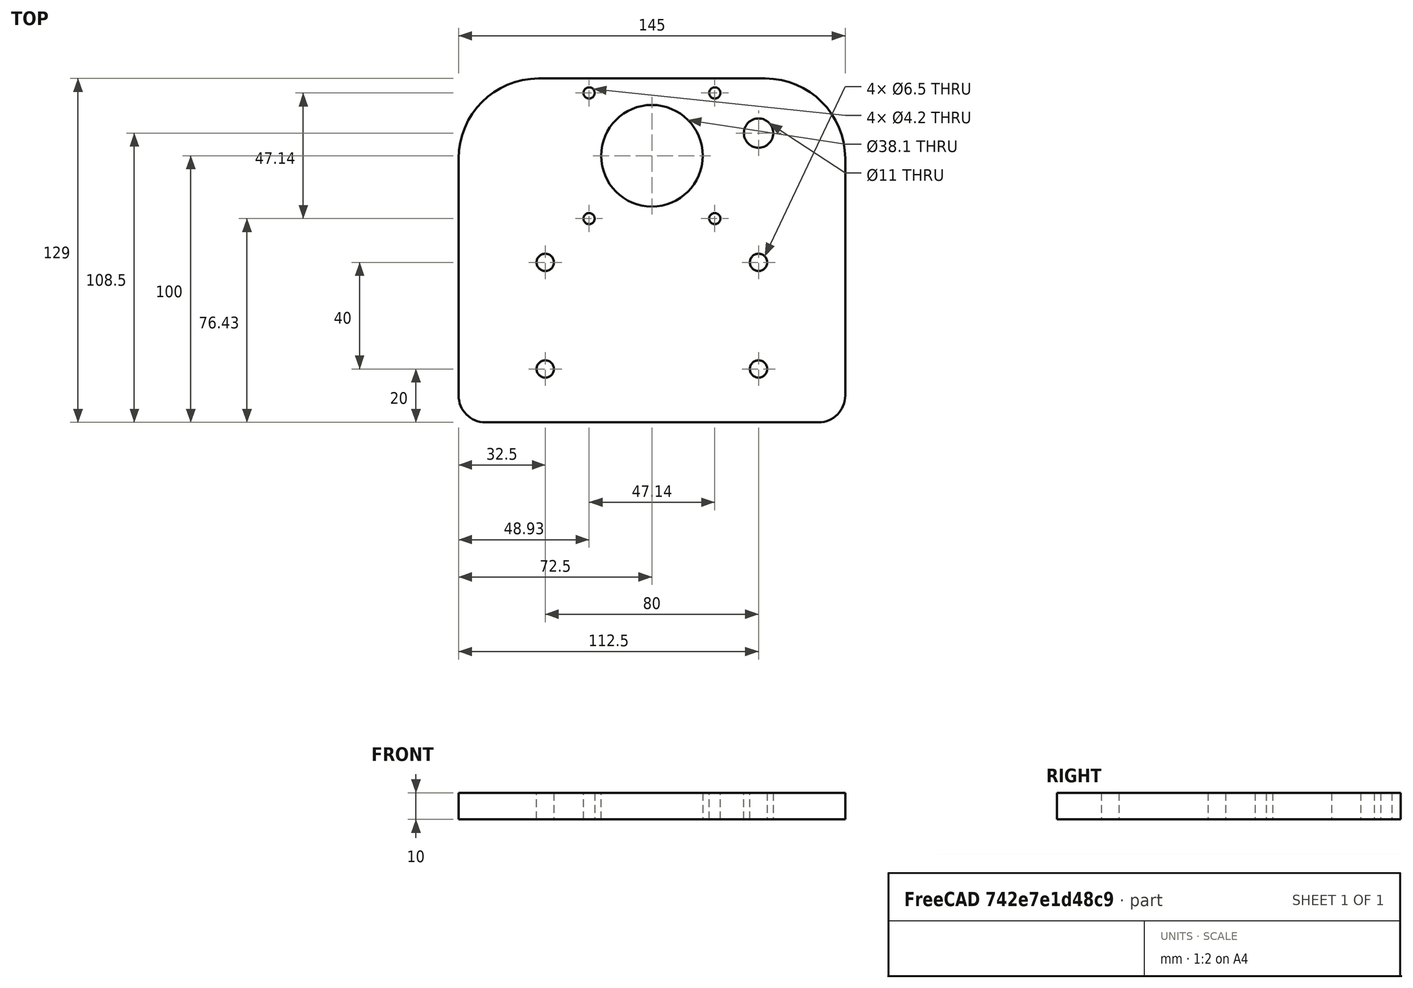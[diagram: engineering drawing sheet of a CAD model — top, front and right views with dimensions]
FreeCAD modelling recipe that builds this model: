
FCSTD DOCUMENT  (FreeCAD 0.21R38887 (Git))
Label: ПластинаY2
License: All rights reserved
LicenseURL: http://en.wikipedia.org/wiki/All_rights_reserved
objects: App::Link×3, Sketcher::SketchObject×1, PartDesign::Pad×1, PartDesign::Body×1
note: 6 computed .brp shape members not serialized (recipe doc carries the construction recipe); baked Part::Feature solids carry a one-line shape summary decoded from their .brp
EXTERNAL_REF file=../../../ТаблицаПараметров.FCStd obj=Spreadsheet
EXTERNAL_REF file=../../../ТаблицаПараметров.FCStd obj=Spreadsheet007
EXTERNAL_REF file=../../../ТаблицаПараметров.FCStd obj=Spreadsheet009

FEATURE [Sketcher::SketchObject] Sketch
  ArcFitTolerance = 0
  ExternalBSplineMaxDegree = 0
  ExternalBSplineTolerance = 0
  FullyConstrained = true
  InternalTolerance = 1e-06
  InvalidShape = false
  MakeInternals = false
  TreeRank = 220
  ValidateShape = false
  expr: Constraints[0] = <<Link002(NEMA23Table)>>.PosadkaMotor
  expr: Constraints[1] = <<ТаблицаПараметров>>#<<ПластиныY>>.Len1
  expr: Constraints[2] = <<ТаблицаПараметров>>#<<ПластиныY>>.Heigh1
  expr: Constraints[37] = <<Link001(Профиль)>>.HTpaz1
  expr: Constraints[38] = <<Link001(Профиль)>>.HTpaz2
  expr: Constraints[42] = <<Link002(NEMA23Table)>>.diamRezba
  expr: Constraints[51] = <<Link002(NEMA23Table)>>.DistOtv
  expr: Constraints[52] = <<Link002(NEMA23Table)>>.DistOtv
  expr: Constraints[54] = <<Link(ПластиныY)>>.Heigh2
  sketch-geometry (19):
    g0: ArcOfCircle CenterX=62.5 CenterY=10 CenterZ=0 NormalX=0 NormalY=0 NormalZ=1 AngleXU=0 Radius=10 StartAngle=4.71239 EndAngle=6.28319
    g1: LineSegment StartX=-72.5 StartY=99 StartZ=0 EndX=-72.5 EndY=10 EndZ=0
    g2: ArcOfCircle CenterX=-62.5 CenterY=10 CenterZ=0 NormalX=0 NormalY=0 NormalZ=1 AngleXU=0 Radius=10 StartAngle=3.14159 EndAngle=4.71239
    g3: ArcOfCircle CenterX=-42.5 CenterY=99 CenterZ=0 NormalX=0 NormalY=0 NormalZ=1 AngleXU=0 Radius=30 StartAngle=1.5708 EndAngle=3.14159
    g4: ArcOfCircle CenterX=42.5 CenterY=99 CenterZ=0 NormalX=0 NormalY=0 NormalZ=1 AngleXU=0 Radius=30 StartAngle=4e-16 EndAngle=1.5708
    g5: Circle CenterX=0 CenterY=100 CenterZ=0 NormalX=0 NormalY=0 NormalZ=-1 AngleXU=0 Radius=19.05
    g6: Circle CenterX=-40 CenterY=60 CenterZ=0 NormalX=0 NormalY=0 NormalZ=-1 AngleXU=0 Radius=3.25
    g7: Circle CenterX=40 CenterY=60 CenterZ=0 NormalX=0 NormalY=0 NormalZ=-1 AngleXU=0 Radius=3.25
    g8: Circle CenterX=40 CenterY=20 CenterZ=0 NormalX=0 NormalY=0 NormalZ=-1 AngleXU=0 Radius=3.25
    g9: Circle CenterX=-40 CenterY=20 CenterZ=0 NormalX=0 NormalY=0 NormalZ=-1 AngleXU=0 Radius=3.25
    g10: Circle CenterX=-23.57 CenterY=76.43 CenterZ=0 NormalX=0 NormalY=0 NormalZ=-1 AngleXU=0 Radius=2.1
    g11: Circle CenterX=23.57 CenterY=123.57 CenterZ=0 NormalX=0 NormalY=0 NormalZ=-1 AngleXU=0 Radius=2.1
    g12: Circle CenterX=-23.57 CenterY=123.57 CenterZ=0 NormalX=0 NormalY=0 NormalZ=-1 AngleXU=0 Radius=2.1
    g13: Circle CenterX=40 CenterY=108.5 CenterZ=0 NormalX=0 NormalY=0 NormalZ=-1 AngleXU=0 Radius=5.5
    g14: LineSegment StartX=42.5 StartY=129 StartZ=0 EndX=-42.5 EndY=129 EndZ=0
    g15: LineSegment StartX=72.5 StartY=10 StartZ=0 EndX=72.5 EndY=99 EndZ=0
    g16: LineSegment StartX=-62.5 StartY=7.1e-15 StartZ=0 EndX=62.5 EndY=-2.49e-14 EndZ=0
    g17: Circle [constr] CenterX=0 CenterY=100 CenterZ=0 NormalX=0 NormalY=0 NormalZ=1 AngleXU=0 Radius=33.333
    g18: Circle CenterX=23.57 CenterY=76.43 CenterZ=0 NormalX=0 NormalY=0 NormalZ=1 AngleXU=0 Radius=2.1
  constraints (58):
    c: Diameter(g5) = 38.1
    c: DistanceX(g1,g0) = 145
    c: DistanceY(g2,g3) = 129
    c: Equal(g3,g4)
    c: Radius(g3) = 30
    c: Equal(g2,g0)
    c: Radius(g2) = 10
    c: Equal(g15,g1)
    c: Vertical(g1)
    c: Vertical(g15)
    c: Horizontal(g14)
    c: Coincident(g1,g2)
    c: Coincident(g16,g2)
    c: Coincident(g0,g16)
    c: Coincident(g0,g15)
    c: Horizontal(g0,g0)
    c: Vertical(g0,g0)
    c: Horizontal(g1,g2)
    c: Vertical(g2,g2)
    c: Coincident(g1,g3)
    c: Coincident(g3,g14)
    c: Horizontal(g3,g1)
    c: Vertical(g3,g3)
    c: Coincident(g4,g15)
    c: Coincident(g4,g14)
    c: Vertical(g4,g4)
    c: Symmetric(g2,g0,g-2)
    c: PointOnObject(g0,g-1)
    c: Vertical(g6,g9)
    c: Horizontal(g7,g6)
    c: Vertical(g7,g8)
    c: Equal(g6,g9)
    c: Equal(g6,g8)
    c: Equal(g6,g7)
    c: Diameter(g6) = 6.5
    c: DistanceX(g9,g8) = 80
    c: Symmetric(g9,g8,g-2)
    c: DistanceY(g-1,g9) = 20
    c: DistanceY(g-1,g6) = 60
    c: Diameter(g13) = 11
    c: Equal(g10,g11)
    c: Equal(g10,g12)
    c: Diameter(g10) = 4.2
    c: PointOnObject(g10,g17)
    c: PointOnObject(g12,g17)
    c: PointOnObject(g11,g17)
    c: Horizontal(g12,g11)
    c: Vertical(g10,g12)
    c: DistanceY(g5,g13) = 8.5
    c: DistanceX(g5,g13) = 40
    c: Coincident(g5,g17)
    c: DistanceX(g12,g11) = 47.14
    c: DistanceY(g10,g12) = 47.14
    c: PointOnObject(g5,g-2)
    c: DistanceY(g-1,g5) = 100
    c: Equal(g10,g18)
    c: Horizontal(g10,g18)
    c: PointOnObject(g18,g17)
FEATURE [App::Link] Link  label="Link(ПластиныY)"
  AutoLinkLabel = true
  AutoPlacement = true
  LinkedObject = -> <external ../../../ТаблицаПараметров.FCStd>#Spreadsheet007
  SyncGroupVisibility = false
  TreeRank = 225
  _LinkVersion = 1
FEATURE [App::Link] Link001  label="Link001(Профиль)"
  AutoLinkLabel = true
  AutoPlacement = true
  LinkedObject = -> <external ../../../ТаблицаПараметров.FCStd>#Spreadsheet
  SyncGroupVisibility = false
  TreeRank = 226
  _LinkVersion = 1
FEATURE [PartDesign::Pad] Pad
  AddSubType = 0
  AlongSketchNormal = false
  AutoTaperInnerAngle = true
  CheckUpToFaceLimits = true
  ClaimChildren = false
  Direction = (0,0,1)
  Fit = 0
  FitJoin = 0
  InnerFit = 0
  InnerFitJoin = 0
  InvalidShape = false
  Length = 10
  Length2 = 10
  Linearize = true
  NewSolid = false
  Profile = -> Sketch
  ReferenceAxis = -> Sketch [N_Axis]
  Suppress = false
  TaperInnerAngle = 0
  TaperInnerAngleRev = 0
  TreeRank = 227
  Type = 0
  ValidateShape = true
  _ProfileBasedVersion = 1
FEATURE [PartDesign::Body] Body  label="ПластинаY2"
  AutoGroupSolids = false
  ClaimAllChildren = false
  ExportMode = 0
  Group = -> [Sketch,Pad]
  InvalidShape = false
  Origin = -> Origin
  Tip = -> Pad
  TreeRank = 222
  ValidateShape = false
  _ExportChildren = -> [Pad]
  _GroupVersion = 1
FEATURE [App::Link] Link002  label="Link002(NEMA23Table)"
  AutoLinkLabel = true
  AutoPlacement = true
  LinkedObject = -> <external ../../../ТаблицаПараметров.FCStd>#Spreadsheet009
  SyncGroupVisibility = false
  TreeRank = 228
  _LinkVersion = 1

RESOLVED EXTERNAL PARTS (link-assembly join: the EXTERNAL_REF files above that resolve inside this repo's crawl, each included once):
---- part ../../../ТаблицаПараметров.FCStd = doc fcstd_60ae2dd5e8f4 ----
FCSTD DOCUMENT  (FreeCAD 0.21R38887 (Git))
Label: ТаблицаПараметров
License: All rights reserved
LicenseURL: http://en.wikipedia.org/wiki/All_rights_reserved
objects: Spreadsheet::Sheet×9
EXTERNAL_REF file=ЧастиСтанка/Станина/Деталі/NEMA23.FCStd obj=Assembly

FEATURE [Spreadsheet::Sheet] Spreadsheet  label="Профиль"
  PythonMode = false
  ShowCells = 0
  TreeRank = 1
  cells = A2=ДлинаПрофиля; B2(Dlina)==<<ТаблСтанина>>.ShirinaStaninu; A3=ШагОтверстийСоединения; B3(ShagOtv)=100; A4=ДиаметрОтверстия; B4(DiametrOtvSoed)=4; A6=Перша висота Т пазу; B6(HTpaz1)=20; A7=Друга висота Т пазу; B7(HTpaz2)=60; A8=КоличествоОтвСоединения; B8(HoleNumberSoed)==trunc(Dlina / ShagOtv) - 1; A9=ДлинаМасиваСоед; B9(DlinaMasivaSoed)==ShagOtv * HoleNumberSoed; A10=ОтступОтКрая; B10(OtstupRels)==(Dlina - DlinaMasivaSoed) / 2
FEATURE [Spreadsheet::Sheet] Spreadsheet001  label="ТаблСтанина"
  PythonMode = false
  ShowCells = 0
  TreeRank = 0
  cells = A2=Ширина; B2(ShirinaStaninu)=480; A3=Количество палок профиля; B3(NumberProfileBody)=10; A4=Высота; B4(RazmerProfilja)=80; A5=Глубина; B5(GlubinaStaninu)==RazmerProfilja * NumberProfileBody
FEATURE [Spreadsheet::Sheet] Spreadsheet002  label="Ролик"
  PythonMode = false
  ShowCells = 0
  TreeRank = 1
  cells = A7=Высота под подшипник; B7(dimH3)==dimH1 + dimH2; C7=висота   подш + висота шайби; A8=Длина общая (без шайб); B8(dimL1)=222; C8=Final lenght; A9=ball radius; B9(ball_radius)==(<<Ролик>>.dimD2 / 2 - <<Ролик>>.diamPodsh / 2) / 3; C9=alpha; D9(alpa)==atan(.ball_radius / .ball_pos_radius); A10=R for ball; B10(ball_pos_radius)==(<<Ролик>>.dimD2 / 2 - <<Ролик>>.diamPodsh / 2) / 2 + <<Ролик>>.diamPodsh / 2; C10=number of ball; D10(ball_number)==trunc(360 / (2 * .alpa)); C11=Длинная гайка; G11=Винт; I11=Подшипник; L11=Труба; N11=Шайба; O11=Шпилька; B12=Inner thread; C12=External dim; D12=Thread index; E12=Lenght; F12=ШайбаИндекс; G12=Индекс винта; H12=Длина винта(index); I12=Диам подш; J12=диад внутр подш; K12=Высота подш.; L12=Диам внешн.; M12=Диам внутр.; N12=Высота шайбы; O12=Индекс; A13=DIN6334 table; B13==dbind(РоликY#Assembly.Configuration.All); C13(din6334_D1)==.C14; D13(din6334_Index)==.D14; E13(din6334_Len)==.E14; F13(ShaibaIndex)==.F14; G13(IndexVinta)==.G14; H13(dlinaVintaInd)==.H14; I13(dimD2)==.I14; J13(diamPodsh)==.J14; K13(dimH1)==.K14; L13(dimD1)==.L14; M13(dimD3)==.M14; N13(dimH2)==.N14; O13(ShpilkaIndex)==.O14; B14=M5v1; C14=8; D14=13; E14=15; F14=6; G14=3; H14=2; I14=14; J14=5; K14=5; L14=16; M14=12; N14=1; O14=7; B15=M5v2; C15=8; D15=13; E15=15; F15=6; G15=3; H15=2; I15=16; J15=5; K15=5; L15=18; M15=14; N15=1; O15=7; B16=M6; C16=10; D16=14; E16=18; F16=7; G16=4; H16=2; I16=19; J16=6; K16=6; L16=21.3; M16=16.1; N16=1.6; O16=8; B17=M8; C17=13; D17=16; E17=24; F17=8; G17=5; H17=3; I17=22; J17=8; K17=7; L17=25; M17=19; N17=1.6; O17=9
  expr: cells.Bind.C13.ZZ13 = tuple(.cells, <<C>> + str(hiddenref(РоликY#Assembly.Configuration) + 14), <<ZZ>> + str(hiddenref(РоликY#Assembly.Configuration) + 14))
FEATURE [Spreadsheet::Sheet] Spreadsheet004  label="ЗащитаТабл"
  PythonMode = false
  ShowCells = 0
  TreeRank = 1
  cells = A2=Ширина 1; B2(dimL1)=45; C2=Слева от П прорези (зависит от опоры и толщины пластины крепления опоры); D2=dimL1; E2=задать формулу; A3=Ширина 2; B3(dimL2)==<<ТаблСтанина>>.GlubinaStaninu; C3=П прорезь Зависит от ширины профиля и количества палок + небольшой зазор (0.2мм); D3=dimL2; A4=Ширина 3; B4(dimL3)==ceil((<<NEMA23Table>>.TotalLen + dimR1 * 2 + 5) / 5) * 5 + 10; C4=Справа от П прорези (motor); D4=dimL3; A5=Высота 1; B5(dimH1)==<<ПластиныY>>.Heigh1; C5=Общая высота защиты; D5=dimH1; E5=висота пластин и защити однакові; A6=Высота 2; B6(dimh2)=80; C6=Высота профиля ; D6=dimh2; A7=Радиус 1; B7(dimR1)==<<Ролик>>.dimD1 / 2; C7=Радиус скругления по углам с роликами; D7=dimR1; A8=Радиус 2; B8(dimR2)=2.5; C8=Крепление роликов; D8=dimR2; A9=Радиус 3; B9(dimR3)==<<ПроставкаYТабл>>.DiamOtvZashitu / 2; C9=Крепление защиты(радиус отверстя); D9=dimR3; A10=Радиус 4; B10(dimR4)=3; C10=Скругление в точках прилегания к профилю; D10=dimR4; A11=Высота 3; B11(dimH3)==<<ПроставкаYТабл>>.Tolshina / 2; C11=Высота винтов крепления защиты; D11=dimH3; A12=ЧислоВинтов1; B12(num1)==<<ПроставкаYТабл>>.NumberHoleZashita; C12=Количество винтов крепления защиты; D12=num1; A13=Шаг1; B13(dimL4)==<<ПроставкаYТабл>>.ShagOtvZash; C13=Расстояние между винтами защиты; D13=dimL4; A14=ДлинаМасива1; B14(dimL5)==num1 * dimL4; C14=Растояние между крайними віинтами защиты; D14=dimL5; A15=Отступ1; B15(dimL6)==(dimL2 - dimL5) / 2; C15=Отступ от начала П прорези до первого винта крепления защиты; D15=dimL6; A16=Толщина листа; B16(toldhinZashita)=1.5; D16=toldhinZashita
FEATURE [Spreadsheet::Sheet] Spreadsheet006  label="ШВП"
  PythonMode = false
  ShowCells = 0
  TreeRank = 2
  cells = A1=ШВП Х; A7=ШВП Y; B7=Длина общая; C7=Диаметр под гайку; D7=Длина резьбы под гайку; E7=Длина вала под крепление; F7=Длина вала под муфту; G7=Диаметр вала под муфту; H7=Шаг ШВП; I7=Диаметр ШВП; B8(lenY)=407; C8(diamYval)=12; D8(lenRezbaYval1)=10; E8(lenValY1)=36; F8(lenMuftaY)=10; G8(diamMuftaY)=10; H8(ShagScrewY)=5; I8(diamSrewY)=16; A12=ШВП Z
FEATURE [Spreadsheet::Sheet] Spreadsheet007  label="ПластиныY"
  PythonMode = false
  ShowCells = 0
  TreeRank = 3
  cells = A1=Параметры пластин для крепления мотора; A3=Ширина пластины; B3(Len1)=145; A4=Висота пластини; B4(Heigh1)=129; A5=ШВП висота ; B5(Heigh2)=100
FEATURE [Spreadsheet::Sheet] Spreadsheet005  label="ПроставкаYТабл"
  Body = -1
  Configuration = 3
  PythonMode = false
  ShowCells = 0
  TreeRank = 5
  cells = A1=Наименование; B1=Значение; C1=Описание параметра; D1=Наименование; E1=Значение; F1=Описание; A2=ДлинаОбщая; D2=Количество точек крепления защиты; E2(NumberHoleZashita)=7; A3=Толщина Проставки; B3(Tolshina)=25; D3=Шаг отверстий под защиту; E3(ShagOtvZash)==<<ТаблСтанина>>.GlubinaStaninu / (NumberHoleZashita + 1); A4=Ширина Проставки; B4(Shirina)=35; D4=ДлинаМасиваКрепежаЗащиты; E4(DlinaMasivaZashita)==NumberHoleZashita * ShagOtvZash; A5=Отступ от края(основание); B5(BodyFirstHole)=20; C5=Отступ от центра; D5(OtstupCenter)==<<ТаблСтанина>>.GlubinaStaninu / 2 - BodyFirstHole; A6=ШагОтверстий; B6(ShagOtverastij)=40; A8=КоличествоОтверстий; B8(HoleNumber)==trunc((<<ТаблСтанина>>.GlubinaStaninu - BodyFirstHole) / ShagOtverastij); A9=ДлинаЛинМасива; B9(DlinaMasiva)==ShagOtverastij * HoleNumber; A11=КоличествоОтвРельс; B11(HoleNumberRels)==trunc(<<ТаблСтанина>>.GlubinaStaninu / ShagRelsa) - 1; A12=ДлинаМасиваРельс; B12(DlinaMasivaRels)==ShagRelsa * HoleNumberRels; A13=ОтступОтКраяРельса; B13(OtstupRels)==(<<ТаблСтанина>>.GlubinaStaninu - DlinaMasivaRels) / 2; A15=КрепежПроставки; B15=ДиаметрОтверстияПодВинт; C15=ДиаметрОтверстия подГоловку; D15=ГлубинаОтверстияПодГоловку; B16(Body_holeDiam)==.B18; C16(BodyHoleDiam)==.C18; D16(BodyHoleGlubina)==.D18; A17=M3; B17=3.2; C17=6; D17=3.4; A18=M4; B18=4.3; C18=8; D18=4.6; A19=M5; B19=5.3; C19=10; D19=5.7; A20=M6; B20=6.4; C20=11; D20=6.8; B24=Ширина Рельсы; C24=Глубина Посадки; D24=Шаг отверстий; E24=Крепление рельсы (индекс резьбы); F24=Длина Винта Крепления; G24=ГлубинаОтверстияПодВИнт; B25(ShirinaPaza)==.B28; C25(GlubunaPaza)==.C28; D25(ShagRelsa)==.D28; E25(indexKreplRels)==.E28; F25(DlinaVintaRels)==.F28; G25(GlubinaOtvRels)==.G28; A26=HGH15; B26=15; C26=4.3; D26=60; E26=11; F26=16; G26=6; A27=HGH20; B27=20; C27=4.6; D27=60; E27=13; F27=16; G27=8; A28=HGH25; B28=23; C28=5.5; D28=60; E28=14; F28=20; G28=8; A32=Крепление боковой защиты; C32=Глубина отверстия под резьбу; D32=Диаметр отверстия в пластине защиты; B33(indexZashita)==.B38; C33(GlubinaOtvZashitu)==.C38; D33(DiamOtvZashitu)==.D38; A34=M3x10; B34=9; C34=10; D34=3.2; A35=M3x12; B35=9; C35=12; D35=3.2; A36=M4x10; B36=11; C36=10; D36=4.3; A37=M4x12; B37=11; C37=12; D37=4.3; A38=M5x10; B38=13; C38=10; D38=5.3; A39=M5x12; B39=13; C39=12; D39=5.3
  expr: Body.Enum = cells[<<A40:|>>]
  expr: Configuration.Enum = cells[<<A17:|>>]
FEATURE [Spreadsheet::Sheet] Spreadsheet009  label="NEMA23Table"
  PythonMode = false
  ShowCells = 0
  TreeRank = 6
  cells = A1=Тип Мотора; B1=Длина мотора; C1=Длина Тела мотора; D1=Длина Вала; E1=Відстань між отворами кріплення; F1=Діаметр кріплення мотора; G1=Діаметр посадки мотора; H1=Діаметр отвору для різьби; B3(TotalLen)==.B12; C3(BodyLen)==.C12; D3(DlinaVala)==.D12; E3(DistOtv)=47.14; F3(DiamOtv)=5; G3(PosadkaMotor)=38.1; H3(diamRezba)=4.2; A4=23HD2304; B4=45; C4=22; D4=63.4; A5=23HD3005; B5=54; C5=31; D5=72.4; A6=23HD4004; B6=56; C6=33; D6=74.4; A7=23HD5401; B7=65; C7=42; D7=83.4; A8=23HD6001; B8=76; C8=53; D8=94.4; A9=23HD8434; B9=100; C9=77; D9=118.4; A10=23HD2601; B10=45; C10=22; D10=63.4; A11=23HD6603; B11=76; C11=53; D11=94.4; A12=23HD7801; B12=82; C12=59; D12=100.4
  expr: cells.Bind.B3.D3 = tuple(.cells, <<B>> + str(hiddenref(NEMA23#Assembly.Base_MotorType) + 4), <<D>> + str(hiddenref(NEMA23#Assembly.Base_MotorType) + 4))
FEATURE [Spreadsheet::Sheet] Spreadsheet010  label="Стол"
  PythonMode = false
  ShowCells = 0
  TreeRank = 7
  cells = A1=Стіл; A2=Ширина столу; B2(StolShirina)=300; A3=Довжина стола; B3(StolDovjuna)=200; A4=Висота столу; B4(StolVusota)=29; A6=Поглиблення під боковий захист; B6(StolPazZahust)=9; A7=Ширина поглиблення під захист; B7(StolPazShuruna)=232; A9=Площадка під каретки; A10=Довжина; B10(StolKaretkaDovjuna)=180; A11=Ширина; B11(StolKaretkuShurina)=222; A12=Ширина каретки; B12(KaretkaShirina)=36; A13=Глибина паза під каретку; B13(KaretkaPaz)=3; A15=Паз під опору; A16=Ширина; B16(OporaShiruna)=72; A17=Довжина; B17(OporaDovjuna)=29; A18=Глибина пазу під опору; B18(OporaPaz)=3
